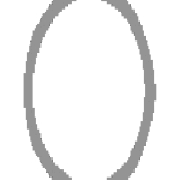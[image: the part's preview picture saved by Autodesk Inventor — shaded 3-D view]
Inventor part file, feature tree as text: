
AUTODESK INVENTOR PART (.ipt)
format: ipt  version: 2021 (Build 250183000, 183)  size: 131,584 bytes
history: native  units: in
note: dims shown in document units (in); Inventor stores cm internally (conversion verified against a paired STEP export)
features: other x4, plane x4, sketch x4, extrude x1, boolean_combine x1
ambient origin geometry x8: Origin, YZ Plane, XZ Plane, XY Plane, X Axis, Y Axis, Z Axis, Center Point
bodies: Solid1 (feature_tree), Body (feature_tree), Solid2 (feature_tree)
feature tree (14):
  other  "Driven Length"
  other  "Frame Generator"
  other  "Start Plane"
  other  "End Plane"
  plane  "Work Plane4"
  plane  "Work Plane5"
  plane  "Work Plane6"
  extrude  "Extrusion3"  Depth=0.065in
  boolean_combine  "Combine1"
  sketch  "Sketch"  dims[d5=5.831in d6=0.12in d7=0.0in d8=90.0deg d9=5.831in d10=0.12in d11=0.0in]
  sketch  "Sketch2"  dims[d0=1.0in d1=0.065in]
  plane  "Work Plane3"
  sketch  "Sketch3"  dims[d2=5.831in]
  sketch  "Sketch4"  dims[d4=-0.0in]
